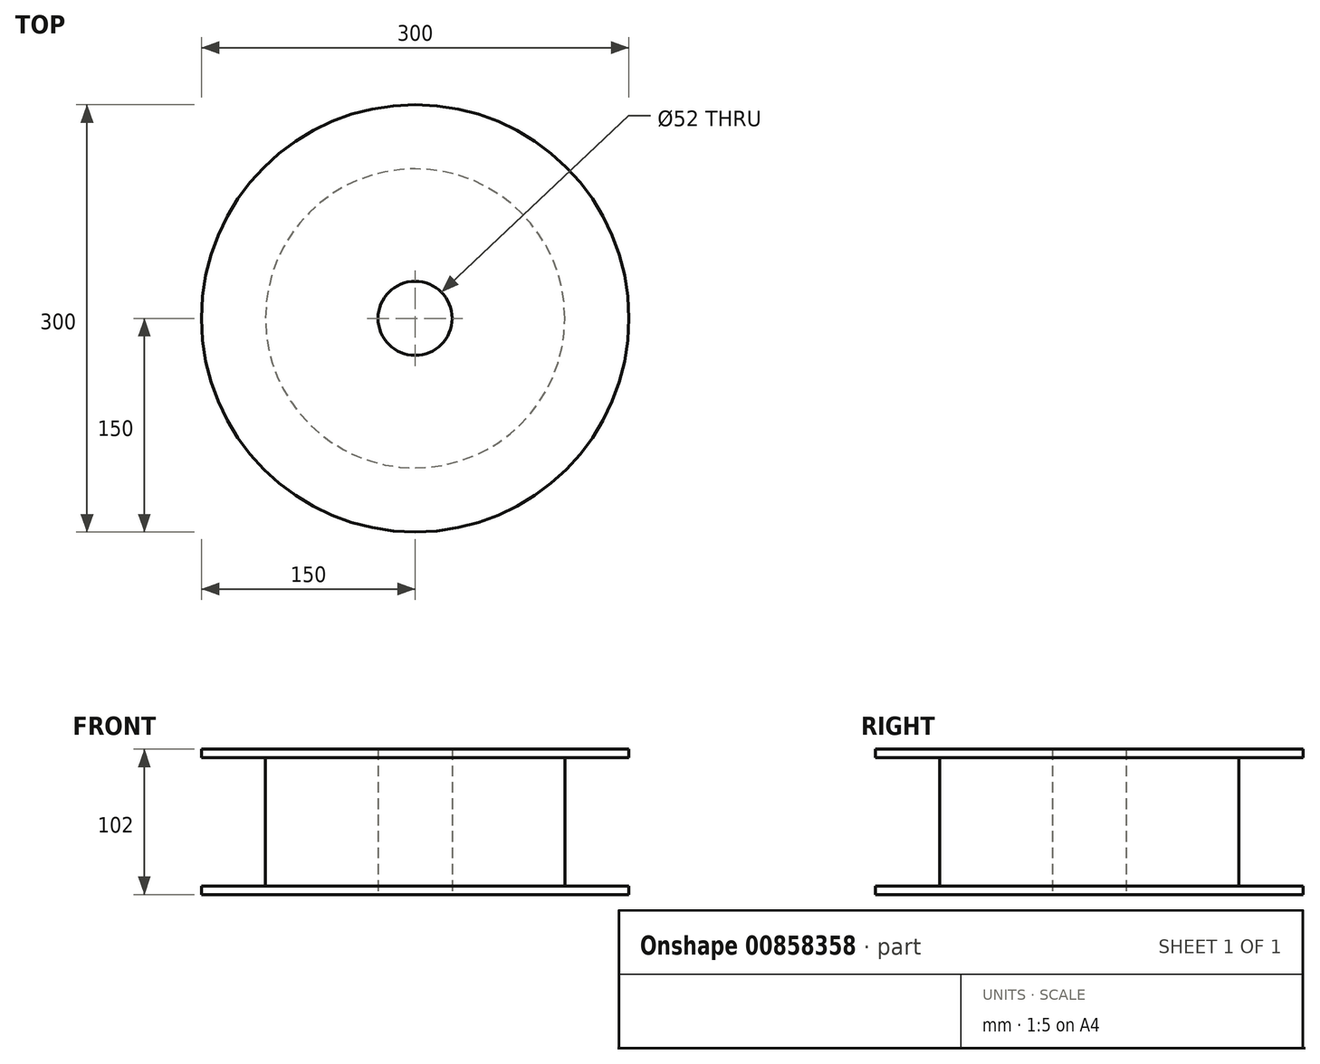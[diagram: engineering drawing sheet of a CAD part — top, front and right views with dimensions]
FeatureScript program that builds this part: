
annotation { "Feature Type Name" : "Feature", "Feature Type Description" : "" }
export const myFeature = defineFeature(function(context is Context, id is Id, definition is map)
    precondition{}
    {
        {
            var Q0;
            Q0=qCreatedBy(makeId("Front.planeOp"),FACE);
            var sketch = newSketch(context, id + "F0", { "sketchPlane" : qUnion([Q0])});
            skLineSegment(sketch, "E0", {"start": v(-150, 51) * mm, "end": v(-150, 45) * mm});
            skLineSegment(sketch, "E1", {"start": v(-150, 45) * mm, "end": v(-105, 45) * mm});
            skLineSegment(sketch, "E2", {"start": v(-105, 45) * mm, "end": v(-105, -45) * mm});
            skLineSegment(sketch, "E3", {"start": v(-105, -45) * mm, "end": v(-150, -45) * mm});
            skLineSegment(sketch, "E4", {"start": v(-150, -45) * mm, "end": v(-150, -51) * mm});
            skLineSegment(sketch, "E5", {"start": v(-150, -51) * mm, "end": v(-26, -51) * mm});
            skLineSegment(sketch, "E6", {"start": v(-150, 51) * mm, "end": v(-26, 51) * mm});
            skLineSegment(sketch, "E7", {"start": v(-26, 51) * mm, "end": v(-26, -51) * mm});
            skLineSegment(sketch, "E8", {"start": v(0, -36.61) * mm, "end": v(0, 31.36) * mm, "construction": true});
            skSolve(sketch);
        }
        {
            var Q0;
            Q0=makeQuery(id+"F0.imprint","IMPRINT",FACE,{"disambiguationData":[TD([[makeQuery(id+"F0.imprint","IMPRINT",EDGE,{"derivedFrom":sQuery(id+"F0.wireOp",EDGE,"E0")}),1.0]])]});
            var Q1;
            Q1 = qConstructionFilter(qBodyType(qCreatedBy(id + "F0" ,EDGE), BodyType.WIRE), ConstructionObject.NO);
            var Q2;
            Q2=sQuery(id+"F0.wireOp",EDGE,"E8");
            revolve(context, id + "F1", {"surfaceOperationType" : NewSurfaceOperationType.NEW, "entities" : qUnion([Q0]), "surfaceEntities" : qUnion([Q1]), "axis" : qUnion([Q2]), "revolveType" : RevolveType.FULL});
        }
    });
